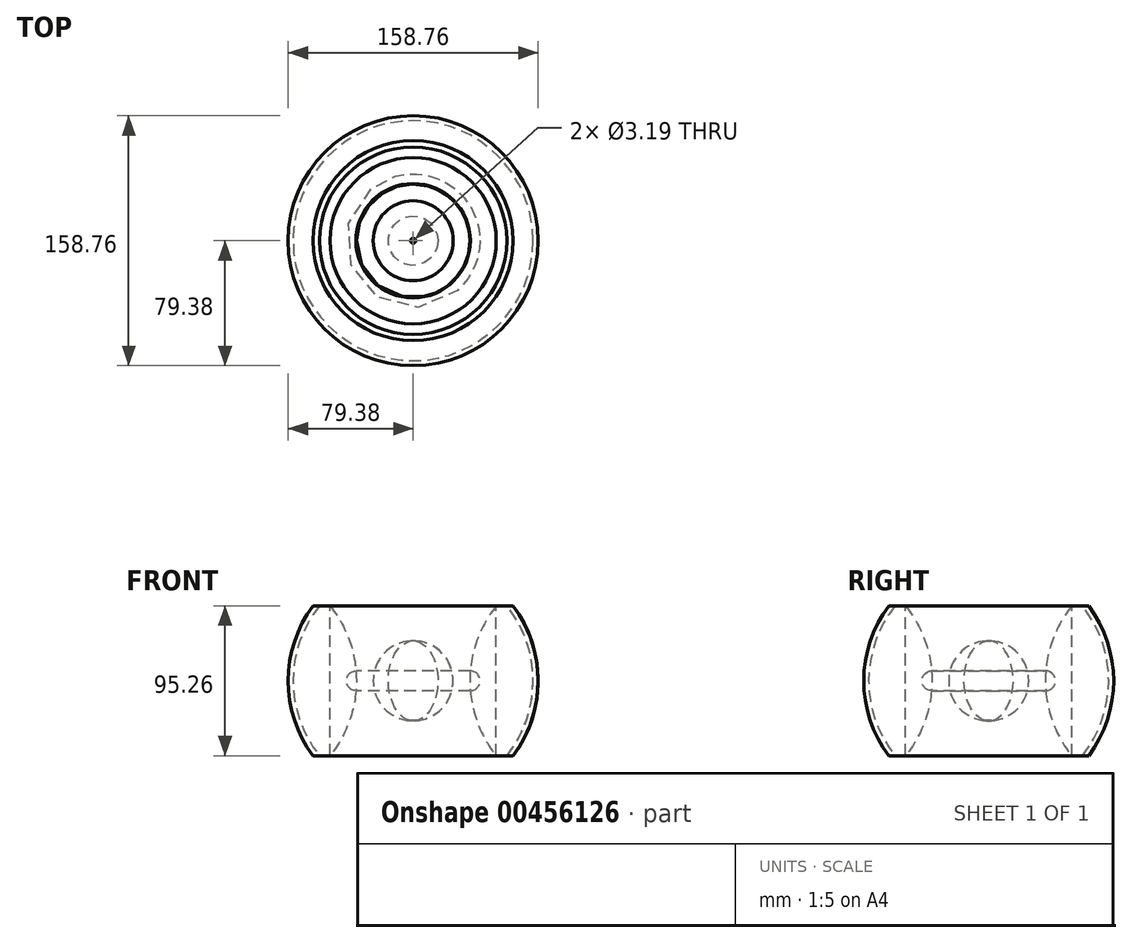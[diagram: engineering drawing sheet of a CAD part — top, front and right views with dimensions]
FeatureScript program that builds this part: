
annotation { "Feature Type Name" : "Feature", "Feature Type Description" : "" }
export const myFeature = defineFeature(function(context is Context, id is Id, definition is map)
    precondition{}
    {
        {
            var Q0;
            Q0=qCreatedBy(makeId("Front.planeOp"),FACE);
            var sketch = newSketch(context, id + "F0", { "sketchPlane" : qUnion([Q0])});
            skArc(sketch, "E0", {"start": v(-1.6, 25.35) * mm, "mid": v(-25.4, 0) * mm, "end": v(-1.6, -25.35) * mm});
            skEllipticalArc(sketch, "E1", {});
            skLineSegment(sketch, "E2.left", {"start": v(1.6, 25.35) * mm, "end": v(1.6, 25.27) * mm});
            skLineSegment(sketch, "E2.right", {"start": v(-1.6, 25.35) * mm, "end": v(-1.6, 25.27) * mm});
            skEllipticalArc(sketch, "E3.trimOffspring", {});
            skArc(sketch, "E4.trimOffspring", {"start": v(1.6, -25.35) * mm, "mid": v(25.4, 0) * mm, "end": v(1.6, 25.35) * mm});
            skLineSegment(sketch, "E5.trimOffspring", {"start": v(-1.6, -25.27) * mm, "end": v(-1.6, -25.35) * mm});
            skLineSegment(sketch, "E6.trimOffspring", {"start": v(1.6, -25.27) * mm, "end": v(1.6, -25.35) * mm});
            skArc(sketch, "E7", {"start": v(-1.6, 26.94) * mm, "mid": v(-26.99, 0) * mm, "end": v(-1.6, -26.94) * mm});
            skLineSegment(sketch, "E8.left", {"start": v(1.6, -25.27) * mm, "end": v(1.6, -26.94) * mm});
            skLineSegment(sketch, "E8.right", {"start": v(-1.6, -25.27) * mm, "end": v(-1.6, -26.94) * mm});
            skLineSegment(sketch, "E9.left", {"start": v(-1.6, 25.35) * mm, "end": v(-1.6, 26.94) * mm});
            skLineSegment(sketch, "E9.right", {"start": v(1.6, 25.35) * mm, "end": v(1.6, 26.94) * mm});
            skArc(sketch, "E10.trimOffspring", {"start": v(1.6, -26.94) * mm, "mid": v(26.99, 0) * mm, "end": v(1.6, 26.94) * mm});
            skLineSegment(sketch, "E11.trimOffspring", {"start": v(12.7, -14.93) * mm, "end": v(12.7, 14.93) * mm});
            skPoint(sketch, "E12.center.orphan", {"position": v(-15.7, 0) * mm});
            skArc(sketch, "E13", {"start": v(-12.7, 14.93) * mm, "mid": v(-13.69, 0) * mm, "end": v(-12.7, -14.93) * mm});
            const initialGuessF0  = {"E1": [0, 0, 0, 1, 0.0254, 0.0156983938, 0.10165024877454586, 3.0399424048152475], "E3.trimOffspring": [0, 0, 0, 1, 0.0254, 0.0156983938, 3.2432429023643383, 6.18153505840504]};
            skSetInitialGuess(sketch, initialGuessF0);
            skSolve(sketch);
        }
        {
            var Q0;
            Q0=qCreatedBy(makeId("Front.planeOp"),FACE);
            var sketch = newSketch(context, id + "F1", { "sketchPlane" : qUnion([Q0])});
            skLineSegment(sketch, "E14", {"start": v(0, 25.46) * mm, "end": v(0, -25.29) * mm});
            skSolve(sketch);
        }
        {
            var Q0;
            Q0=makeQuery(id+"F0.imprint","IMPRINT",FACE,{"disambiguationData":[TD([[makeQuery(id+"F0.imprint","IMPRINT",EDGE,{"derivedFrom":sQuery(id+"F0.wireOp",EDGE,"E0")}),1.0]])]});
            var Q1;
            Q1=sQuery(id+"F1.wireOp",EDGE,"E14");
            revolve(context, id + "F2", {"entities" : qUnion([Q0]), "axis" : qUnion([Q1]), "revolveType" : RevolveType.FULL});
        }
        {
            var Q0;
            Q0=qCreatedBy(makeId("Front.planeOp"),FACE);
            var sketch = newSketch(context, id + "F3", { "sketchPlane" : qUnion([Q0])});
            skArc(sketch, "E15", {"start": v(0, 26.99) * mm, "mid": v(-26.99, 0) * mm, "end": v(0, -26.99) * mm});
            skLineSegment(sketch, "E16", {"start": v(0, 26.99) * mm, "end": v(0, -26.99) * mm});
            skSolve(sketch);
        }
        {
            var Q0;
            Q0=qCreatedBy(makeId("Front.planeOp"),FACE);
            var sketch = newSketch(context, id + "F4", { "sketchPlane" : qUnion([Q0])});
            skCircle(sketch, "E17", {"center": v(0, 0) * mm, "radius": 25.4 * mm});
            skLineSegment(sketch, "E18.bottom", {"start": v(-1.59, 27.1) * mm, "end": v(1.59, 27.1) * mm});
            skLineSegment(sketch, "E18.top", {"start": v(-1.59, -27.1) * mm, "end": v(1.59, -27.1) * mm});
            skLineSegment(sketch, "E18.left", {"start": v(-1.59, 27.1) * mm, "end": v(-1.59, -27.1) * mm});
            skLineSegment(sketch, "E18.right", {"start": v(1.59, 27.1) * mm, "end": v(1.59, -27.1) * mm});
            skEllipse(sketch, "E19", {"center": v(0, 0) * mm, "majorRadius": 25.4 * mm, "minorRadius": 20.64 * mm, "majorAxis": v(0, 1)});
            skLineSegment(sketch, "E20.bottom", {"start": v(-19.24, 29.53) * mm, "end": v(19.24, 29.53) * mm});
            skLineSegment(sketch, "E20.top", {"start": v(-19.24, -29.53) * mm, "end": v(19.24, -29.53) * mm});
            skLineSegment(sketch, "E20.left", {"start": v(-19.24, 29.53) * mm, "end": v(-19.24, -29.53) * mm});
            skLineSegment(sketch, "E20.right", {"start": v(19.24, 29.53) * mm, "end": v(19.24, -29.53) * mm});
            skSolve(sketch);
        }
        {
            var Q0;
            Q0=qCreatedBy(makeId("Front.planeOp"),FACE);
            var sketch = newSketch(context, id + "F5", { "sketchPlane" : qUnion([Q0])});
            skArc(sketch, "E21", {"start": v(-1.2, 25.37) * mm, "mid": v(0, -25.4) * mm, "end": v(1.2, 25.37) * mm});
            skArc(sketch, "E22", {"start": v(-1.2, 17.87) * mm, "mid": v(0, -17.9) * mm, "end": v(1.2, 17.87) * mm});
            skLineSegment(sketch, "E23.left", {"start": v(1.2, 25.37) * mm, "end": v(1.2, 17.87) * mm});
            skLineSegment(sketch, "E23.right", {"start": v(-1.2, 25.37) * mm, "end": v(-1.2, 17.87) * mm});
            skPoint(sketch, "E24.orphan", {"position": v(-1.2, 31.78) * mm});
            skPoint(sketch, "E25.orphan", {"position": v(1.2, 31.78) * mm});
            skLineSegment(sketch, "E26.trimOffspring", {"start": v(-1.2, -17.87) * mm, "end": v(-1.2, -25.37) * mm});
            skLineSegment(sketch, "E27.trimOffspring", {"start": v(1.2, -17.87) * mm, "end": v(1.2, -25.37) * mm});
            skPoint(sketch, "E23.top.end.orphan", {"position": v(-1.2, -31.78) * mm});
            skPoint(sketch, "E23.top.start.orphan", {"position": v(1.2, -31.78) * mm});
            skSolve(sketch);
        }
        {
            var Q0;
            Q0=qCreatedBy(makeId("Front.planeOp"),FACE);
            var sketch = newSketch(context, id + "F6", { "sketchPlane" : qUnion([Q0])});
            skCircle(sketch, "E28", {"center": v(0, 0) * mm, "radius": 25.4 * mm});
            skLineSegment(sketch, "E29", {"start": v(0, 25.4) * mm, "end": v(0, -25.4) * mm});
            skSolve(sketch);
        }
        {
            var Q0;
            Q0=qCreatedBy(makeId("Front.planeOp"),FACE);
            var sketch = newSketch(context, id + "F7", { "sketchPlane" : qUnion([Q0])});
            skCircle(sketch, "E30", {"center": v(0, 0) * mm, "radius": 25.4 * mm});
            skCircle(sketch, "E31", {"center": v(0, 0) * mm, "radius": 26.99 * mm});
            skLineSegment(sketch, "E32.bottom", {"start": v(-19.08, 19.08) * mm, "end": v(19.08, 19.08) * mm});
            skLineSegment(sketch, "E32.top", {"start": v(-19.08, -19.08) * mm, "end": v(19.08, -19.08) * mm});
            skLineSegment(sketch, "E32.left", {"start": v(-19.08, 19.08) * mm, "end": v(-19.08, -19.08) * mm});
            skLineSegment(sketch, "E32.right", {"start": v(19.08, 19.08) * mm, "end": v(19.08, -19.08) * mm});
            skLineSegment(sketch, "E33", {"start": v(-19.08, 19.08) * mm, "end": v(0, 0) * mm});
            skLineSegment(sketch, "E34", {"start": v(0, 0) * mm, "end": v(-19.08, -19.08) * mm});
            skLineSegment(sketch, "E35", {"start": v(0, 0) * mm, "end": v(-38.17, 0) * mm});
            skCircle(sketch, "E36", {"center": v(-38.17, 0) * mm, "radius": 26.99 * mm});
            skLineSegment(sketch, "E37.bottom", {"start": v(26.54, 15.97) * mm, "end": v(-21.75, 15.97) * mm});
            skLineSegment(sketch, "E37.top", {"start": v(26.54, -15.97) * mm, "end": v(-21.75, -15.97) * mm});
            skLineSegment(sketch, "E37.left", {"start": v(26.54, 15.97) * mm, "end": v(26.54, -15.97) * mm});
            skPoint(sketch, "E37.middle", {"position": v(-11.18, 0) * mm});
            skPoint(sketch, "E37.right.end.orphan", {"position": v(-48.9, -15.97) * mm});
            skPoint(sketch, "E38.orphan", {"position": v(-48.9, 15.97) * mm});
            skLineSegment(sketch, "E39", {"start": v(-21.75, 15.97) * mm, "end": v(-19.75, 15.97) * mm});
            skLineSegment(sketch, "E40", {"start": v(-19.75, 15.97) * mm, "end": v(-17.73, 15.97) * mm});
            skCircle(sketch, "E41", {"center": v(-38.17, 0) * mm, "radius": 25.94 * mm});
            skLineSegment(sketch, "E42", {"start": v(-17.73, 15.97) * mm, "end": v(-17.73, -15.97) * mm});
            skArc(sketch, "E43", {"start": v(-17.73, -15.97) * mm, "mid": v(-16.36, 0) * mm, "end": v(-17.73, 15.97) * mm});
            skCircle(sketch, "E44", {"center": v(-16.36, 0) * mm, "radius": 1.59 * mm});
            skSolve(sketch);
        }
        {
            var Q0;
            Q0=qCreatedBy(makeId("Front.planeOp"),FACE);
            var sketch = newSketch(context, id + "F8", { "sketchPlane" : qUnion([Q0])});
            skCircle(sketch, "E45", {"center": v(0, 0) * mm, "radius": 76.2 * mm});
            skCircle(sketch, "E46", {"center": v(0, 0) * mm, "radius": 79.38 * mm});
            skLineSegment(sketch, "E47.bottom", {"start": v(-56.12, 56.13) * mm, "end": v(56.12, 56.13) * mm});
            skLineSegment(sketch, "E47.top", {"start": v(-56.12, -56.13) * mm, "end": v(56.12, -56.13) * mm});
            skLineSegment(sketch, "E47.left", {"start": v(-56.12, 56.13) * mm, "end": v(-56.12, -56.13) * mm});
            skLineSegment(sketch, "E47.right", {"start": v(56.12, 56.13) * mm, "end": v(56.12, -56.13) * mm});
            skLineSegment(sketch, "E48.bottom", {"start": v(126.73, 47.63) * mm, "end": v(-126.73, 47.63) * mm});
            skLineSegment(sketch, "E48.top", {"start": v(126.73, -47.63) * mm, "end": v(-126.73, -47.63) * mm});
            skLineSegment(sketch, "E48.left", {"start": v(126.73, 47.63) * mm, "end": v(126.73, -47.63) * mm});
            skLineSegment(sketch, "E48.right", {"start": v(-126.73, 47.63) * mm, "end": v(-126.73, -47.63) * mm});
            skLineSegment(sketch, "E49", {"start": v(-56.12, 47.63) * mm, "end": v(-59.48, 47.63) * mm});
            skLineSegment(sketch, "E50", {"start": v(-59.48, 47.63) * mm, "end": v(-56.12, 47.63) * mm});
            skLineSegment(sketch, "E51", {"start": v(-56.12, 47.63) * mm, "end": v(-52.78, 47.63) * mm});
            skLineSegment(sketch, "E52", {"start": v(-52.78, 47.63) * mm, "end": v(-52.78, -47.63) * mm});
            skLineSegment(sketch, "E53", {"start": v(-52.78, -47.63) * mm, "end": v(-59.48, -47.63) * mm});
            skArc(sketch, "E54", {"start": v(-52.78, -47.63) * mm, "mid": v(-36.06, 0) * mm, "end": v(-52.78, 47.63) * mm});
            skCircle(sketch, "E55", {"center": v(-36.06, 0) * mm, "radius": 6.35 * mm});
            skSolve(sketch);
        }
        {
            var Q0;
            {var subQ0=sQuery(id+"F8.wireOp",EDGE,"E48.bottom");var subQ5=sQuery(id+"F8.wireOp",EDGE,"E46");var subQ6=makeQuery(id+"F8.imprint","INTERSECT",VERTEX,{"disambiguationData":[OD(1.0)],"derivedFrom":[subQ5,subQ0]});Q0=makeQuery(id+"F8.imprint","IMPRINT",FACE,{"disambiguationData":[TD([[makeQuery(id+"F8.imprint","IMPRINT",EDGE,{"disambiguationData":[TD([[subQ6,-1.0]])],"derivedFrom":subQ5}),1.0]])]});}
            var Q1;
            Q1=sQuery(id+"F1.wireOp",EDGE,"E14");
            revolve(context, id + "F9", {"entities" : qUnion([Q0]), "axis" : qUnion([Q1]), "revolveType" : RevolveType.FULL});
        }
        {
            var Q0;
            {var subQ0=sQuery(id+"F8.wireOp",EDGE,"E52");Q0=makeQuery(id+"F8.imprint","IMPRINT",FACE,{"disambiguationData":[TD([[makeQuery(id+"F8.imprint","IMPRINT",EDGE,{"derivedFrom":subQ0}),1.0]])]});}
            var Q1;
            {var subQ0=sQuery(id+"F8.wireOp",EDGE,"E51");Q1=makeQuery(id+"F8.imprint","IMPRINT",FACE,{"disambiguationData":[TD([[makeQuery(id+"F8.imprint","IMPRINT",EDGE,{"derivedFrom":subQ0}),-1.0]])]});}
            var Q2;
            {var subQ0=sQuery(id+"F8.wireOp",EDGE,"E50");Q2=makeQuery(id+"F8.imprint","IMPRINT",FACE,{"disambiguationData":[TD([[makeQuery(id+"F8.imprint","IMPRINT",EDGE,{"derivedFrom":subQ0}),-1.0]])]});}
            var Q3;
            Q3=sQuery(id+"F1.wireOp",EDGE,"E14");
            revolve(context, id + "F10", {"entities" : qUnion([Q0, Q1, Q2]), "axis" : qUnion([Q3]), "revolveType" : RevolveType.FULL});
        }
        {
            var Q0;
            {var subQ0=sQuery(id+"F8.wireOp",EDGE,"E55");var subQ1=sQuery(id+"F8.wireOp",EDGE,"E54");var subQ2=makeQuery(id+"F8.imprint","INTERSECT",VERTEX,{"disambiguationData":[OD(0.0)],"derivedFrom":[subQ1,subQ0]});Q0=makeQuery(id+"F8.imprint","IMPRINT",FACE,{"disambiguationData":[TD([[makeQuery(id+"F8.imprint","IMPRINT",EDGE,{"disambiguationData":[TD([[subQ2,-1.0]])],"derivedFrom":subQ1}),1.0]])]});}
            var Q1;
            Q1=sQuery(id+"F1.wireOp",EDGE,"E14");
            revolve(context, id + "F11", {"entities" : qUnion([Q0]), "axis" : qUnion([Q1]), "revolveType" : RevolveType.FULL});
        }
    });
